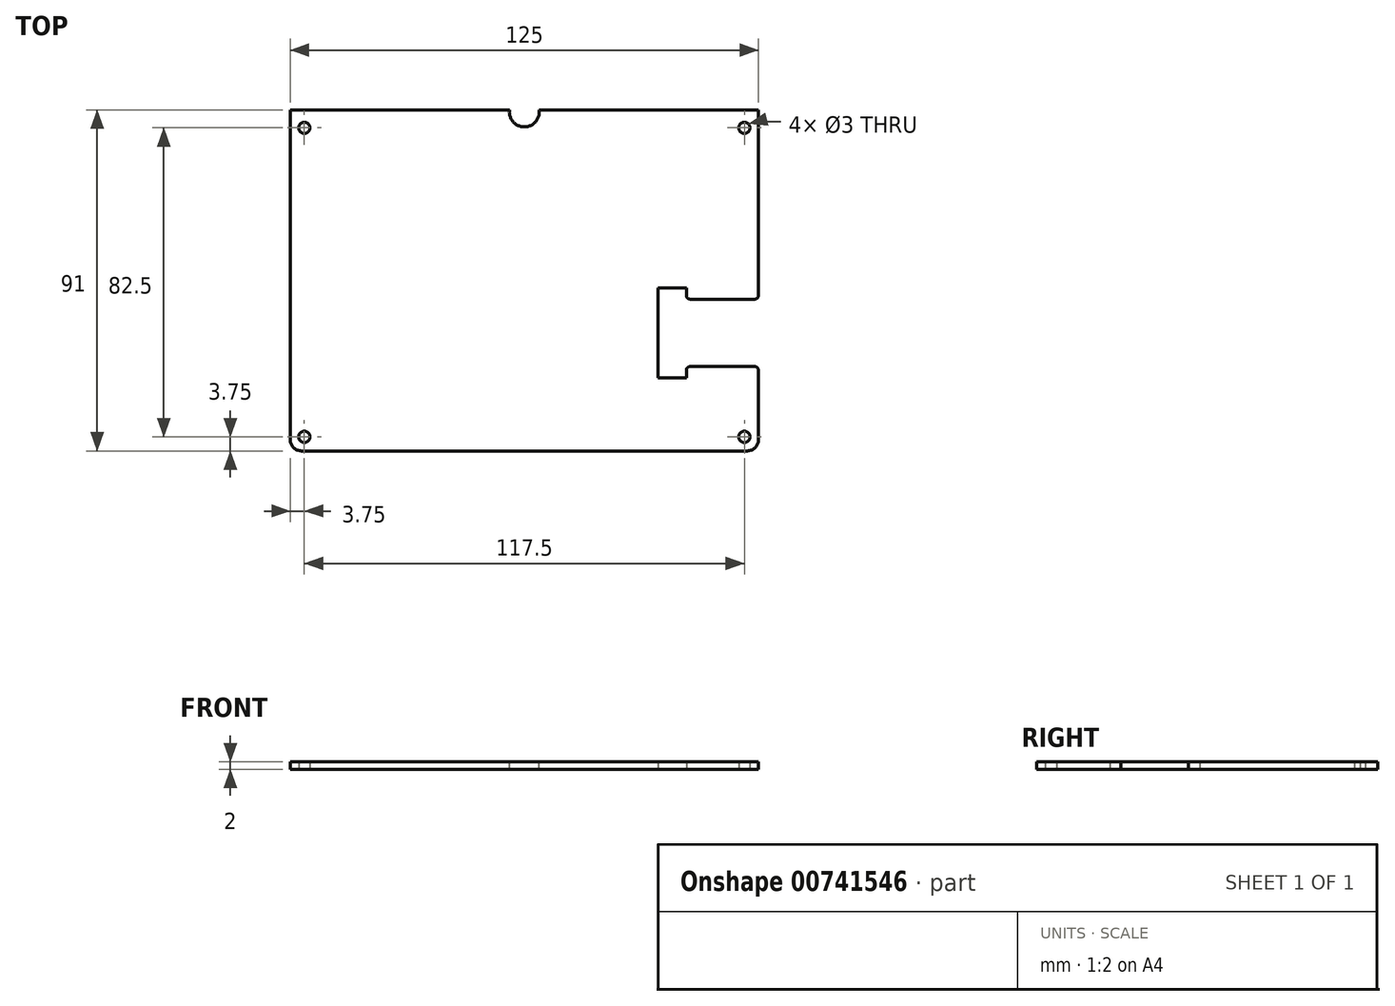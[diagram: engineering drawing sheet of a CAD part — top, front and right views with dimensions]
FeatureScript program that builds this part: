
annotation { "Feature Type Name" : "Feature", "Feature Type Description" : "" }
export const myFeature = defineFeature(function(context is Context, id is Id, definition is map)
    precondition{}
    {
        {
            var Q0;
            Q0=qCreatedBy(makeId("Top.planeOp"),FACE);
            var sketch = newSketch(context, id + "F0", { "sketchPlane" : qUnion([Q0])});
            skLineSegment(sketch, "E0.bottom", {"start": v(-62.5, 45.5) * mm, "end": v(62.5, 45.5) * mm});
            skLineSegment(sketch, "E0.left", {"start": v(-62.5, 45.5) * mm, "end": v(-62.5, -42.5) * mm});
            skPoint(sketch, "E1", {"position": v(-59.5, -42.5) * mm});
            skLineSegment(sketch, "E2", {"start": v(0, 51.35) * mm, "end": v(0, -91.84) * mm, "construction": true});
            skArc(sketch, "E3", {"start": v(-62.5, -42.5) * mm, "mid": v(-61.62, -44.62) * mm, "end": v(-59.5, -45.5) * mm});
            skArc(sketch, "E4.MirrorCS", {"start": v(62.5, -42.5) * mm, "mid": v(61.62, -44.62) * mm, "end": v(59.5, -45.5) * mm});
            skLineSegment(sketch, "E5", {"start": v(-59.5, -45.5) * mm, "end": v(59.5, -45.5) * mm});
            skCircle(sketch, "E6", {"center": v(-58.75, 40.75) * mm, "radius": 1.5 * mm});
            skCircle(sketch, "E7", {"center": v(-58.75, -41.75) * mm, "radius": 1.5 * mm});
            skCircle(sketch, "E8.MirrorC", {"center": v(58.75, 40.75) * mm, "radius": 1.5 * mm});
            skCircle(sketch, "E9.MirrorC", {"center": v(58.75, -41.75) * mm, "radius": 1.5 * mm});
            skLineSegment(sketch, "E10", {"start": v(62.5, -42.5) * mm, "end": v(62.5, -24) * mm});
            skLineSegment(sketch, "E11", {"start": v(61.5, -23) * mm, "end": v(44.25, -23) * mm});
            skLineSegment(sketch, "E12", {"start": v(43.25, -24) * mm, "end": v(43.25, -26) * mm});
            skLineSegment(sketch, "E13", {"start": v(43.25, -26) * mm, "end": v(35.75, -26) * mm});
            skLineSegment(sketch, "E14", {"start": v(35.75, -26) * mm, "end": v(35.75, -2) * mm});
            skLineSegment(sketch, "E15", {"start": v(35.75, -2) * mm, "end": v(43.25, -2) * mm});
            skLineSegment(sketch, "E16", {"start": v(43.25, -2) * mm, "end": v(43.25, -4) * mm});
            skLineSegment(sketch, "E17", {"start": v(44.25, -5) * mm, "end": v(61.5, -5) * mm});
            skLineSegment(sketch, "E18", {"start": v(62.5, -4) * mm, "end": v(62.5, 45.5) * mm});
            skLineSegment(sketch, "E19", {"start": v(77.39, -14) * mm, "end": v(17.88, -14) * mm, "construction": true});
            skPoint(sketch, "E20.visualSharp", {"position": v(43.25, -23) * mm});
            skArc(sketch, "E20.filletArc", {"start": v(44.25, -23) * mm, "mid": v(43.54, -23.3) * mm, "end": v(43.25, -24) * mm});
            skPoint(sketch, "E21.visualSharp", {"position": v(62.5, -23) * mm});
            skArc(sketch, "E21.filletArc", {"start": v(62.5, -24) * mm, "mid": v(62.2, -23.3) * mm, "end": v(61.5, -23) * mm});
            skPoint(sketch, "E22.visualSharp", {"position": v(43.25, -5) * mm});
            skArc(sketch, "E22.filletArc", {"start": v(43.25, -4) * mm, "mid": v(43.54, -4.7) * mm, "end": v(44.25, -5) * mm});
            skPoint(sketch, "E23.visualSharp", {"position": v(62.5, -5) * mm});
            skArc(sketch, "E23.filletArc", {"start": v(61.5, -5) * mm, "mid": v(62.2, -4.7) * mm, "end": v(62.5, -4) * mm});
            skSolve(sketch);
        }
        {
            var Q0;
            Q0=makeQuery(id+"F0.imprint","IMPRINT",FACE,{"disambiguationData":[TD([[makeQuery(id+"F0.imprint","IMPRINT",EDGE,{"derivedFrom":sQuery(id+"F0.wireOp",EDGE,"E0.bottom")}),-1.0]])]});
            extrude(context, id + "F1", {"entities" : qUnion([Q0]), "depth" : 2 * mm, "offsetDistance" : 25 * mm});
        }
        {
            var Q0;
            Q0=makeQuery(id+"F1.opExtrude","CAP_FACE",FACE,{"disambiguationData":[OSD([sQuery(id+"F0.wireOp",EDGE,"E0.bottom"),sQuery(id+"F0.wireOp",EDGE,"E0.left"),sQuery(id+"F0.wireOp",EDGE,"E3"),sQuery(id+"F0.wireOp",EDGE,"E4.MirrorCS"),sQuery(id+"F0.wireOp",EDGE,"E5"),sQuery(id+"F0.wireOp",EDGE,"E6"),sQuery(id+"F0.wireOp",EDGE,"E7"),sQuery(id+"F0.wireOp",EDGE,"E8.MirrorC"),sQuery(id+"F0.wireOp",EDGE,"E9.MirrorC"),sQuery(id+"F0.wireOp",EDGE,"E10"),sQuery(id+"F0.wireOp",EDGE,"E11"),sQuery(id+"F0.wireOp",EDGE,"E12"),sQuery(id+"F0.wireOp",EDGE,"E13"),sQuery(id+"F0.wireOp",EDGE,"E14"),sQuery(id+"F0.wireOp",EDGE,"E15"),sQuery(id+"F0.wireOp",EDGE,"E16"),sQuery(id+"F0.wireOp",EDGE,"E17"),sQuery(id+"F0.wireOp",EDGE,"E18"),sQuery(id+"F0.wireOp",EDGE,"E20.filletArc"),sQuery(id+"F0.wireOp",EDGE,"E21.filletArc"),sQuery(id+"F0.wireOp",EDGE,"E22.filletArc"),sQuery(id+"F0.wireOp",EDGE,"E23.filletArc")])],"isStart":false});
            var sketch = newSketch(context, id + "F2", { "sketchPlane" : qUnion([Q0])});
            skCircle(sketch, "E24", {"center": v(0, 45) * mm, "radius": 4 * mm});
            skLineSegment(sketch, "E25", {"start": v(-4, 45) * mm, "end": v(-4, 49) * mm});
            skLineSegment(sketch, "E26", {"start": v(4, 45) * mm, "end": v(4, 49) * mm});
            skLineSegment(sketch, "E27", {"start": v(-4, 49) * mm, "end": v(4, 49) * mm});
            skSolve(sketch);
        }
        {
            var Q0;
            {var subQ0=sQuery(id+"F2.wireOp",EDGE,"E24");var subQ1=makeQuery(id+"F2.imprint","INTERSECT",VERTEX,{"derivedFrom":[subQ0,sQuery(id+"F2.wireOp",EDGE,"E26")]});Q0=makeQuery(id+"F2.imprint","IMPRINT",FACE,{"disambiguationData":[TD([[makeQuery(id+"F2.imprint","IMPRINT",EDGE,{"disambiguationData":[TD([[subQ1,-1.0]])],"derivedFrom":subQ0}),1.0]])]});}
            var Q1;
            {var subQ0=sQuery(id+"F2.wireOp",EDGE,"E27");var subQ1=sQuery(id+"F2.wireOp",EDGE,"E24");var subQ2=makeQuery(id+"F2.imprint","INTERSECT",VERTEX,{"derivedFrom":[subQ1,subQ0]});Q1=makeQuery(id+"F2.imprint","IMPRINT",FACE,{"disambiguationData":[TD([[makeQuery(id+"F2.imprint","IMPRINT",EDGE,{"disambiguationData":[TD([[subQ2,-1.0]])],"derivedFrom":subQ1}),-1.0]])]});}
            var Q2;
            {var subQ0=sQuery(id+"F2.wireOp",EDGE,"E27");var subQ1=sQuery(id+"F2.wireOp",EDGE,"E24");var subQ2=makeQuery(id+"F2.imprint","INTERSECT",VERTEX,{"derivedFrom":[subQ1,subQ0]});Q2=makeQuery(id+"F2.imprint","IMPRINT",FACE,{"disambiguationData":[TD([[makeQuery(id+"F2.imprint","IMPRINT",EDGE,{"disambiguationData":[TD([[subQ2,1.0]])],"derivedFrom":subQ1}),-1.0]])]});}
            extrude(context, id + "F3", {"entities" : qUnion([Q0, Q1, Q2]), "operationType" : NewBodyOperationType.REMOVE, "endBound" : BoundingType.THROUGH_ALL, "oppositeDirection" : true, "depth" : 25 * mm, "offsetDistance" : 25 * mm});
        }
    });
